# Revit family: okamura_MS36MSN_Lives Pouf_Φ600 H420_1
name_source: partatom
category: Furniture
revit_build: Autodesk Revit 2017 (Build: 20160225_1515(x64)
units: mm (PartAtom-declared; Revit-internal decimal feet)

## family parameters
Always vertical = Yes
Cut with Voids When Loaded = No
OmniClass Number = 23.40.20.00
OmniClass Title = General Furniture and Specialties
Room Calculation Point = No
Shared = No
Work Plane-Based = No

## types (10) — shared parameters
Assembly Code = E2020200
D = 600 mm
H = 420 mm  [stored 1.37795 ft]
Keynote = 12490
Kind = Stool
Manufacturer = Okamura Corporation
Product Categories = Collaboration
Product Number = MS36MSN
URL = http://www.okamura.co.jp
W = 600 mm

## per-type parameters (varying)
| type | Ball edge | Body | Groove | Tag |
| FNW2（Beige） | okm_FKY7 | okm_FXW2 | okm_XW2 | okm_P346 |
| FNW3（Dark brown） | okm_FKY3 | okm_FXW3 | okm_XW3 | okm_P346 |
| FNW1（Gray） | okm_FKY2 | okm_FXW1 | okm_XW1 | okm_P601 |
| FNW4（Indigo） | okm_FKY4 | okm_FXW4 | okm_XW4 | okm_P601 |
| FNW9（Sage） | okm_FKY6 | okm_FXW9 | okm_XW9 | okm_P601 |
| FNW5（Dark green） | okm_FKY5 | okm_FXW5 | okm_XW5 | okm_PE76 |
| FNW7（Yellow） | okm_FKY9 | okm_FXW7 | okm_XW7 | okm_PE76 |
| FNW6（Terracotta） | okm_FKY8 | okm_FXW6 | okm_XW6 | okm_PE77 |
| FNW8（Pale pink） | okm_FKZ7 | okm_FXW8 | okm_XW8 | okm_PE77 |
| FNW0（Dark gray） | okm_FKY1 | okm_FXW0 | okm_XW0 | okm_P601 |

note: [stored X ft] marks values corroborated as IEEE doubles in the binary element streams (Revit-internal decimal feet)
